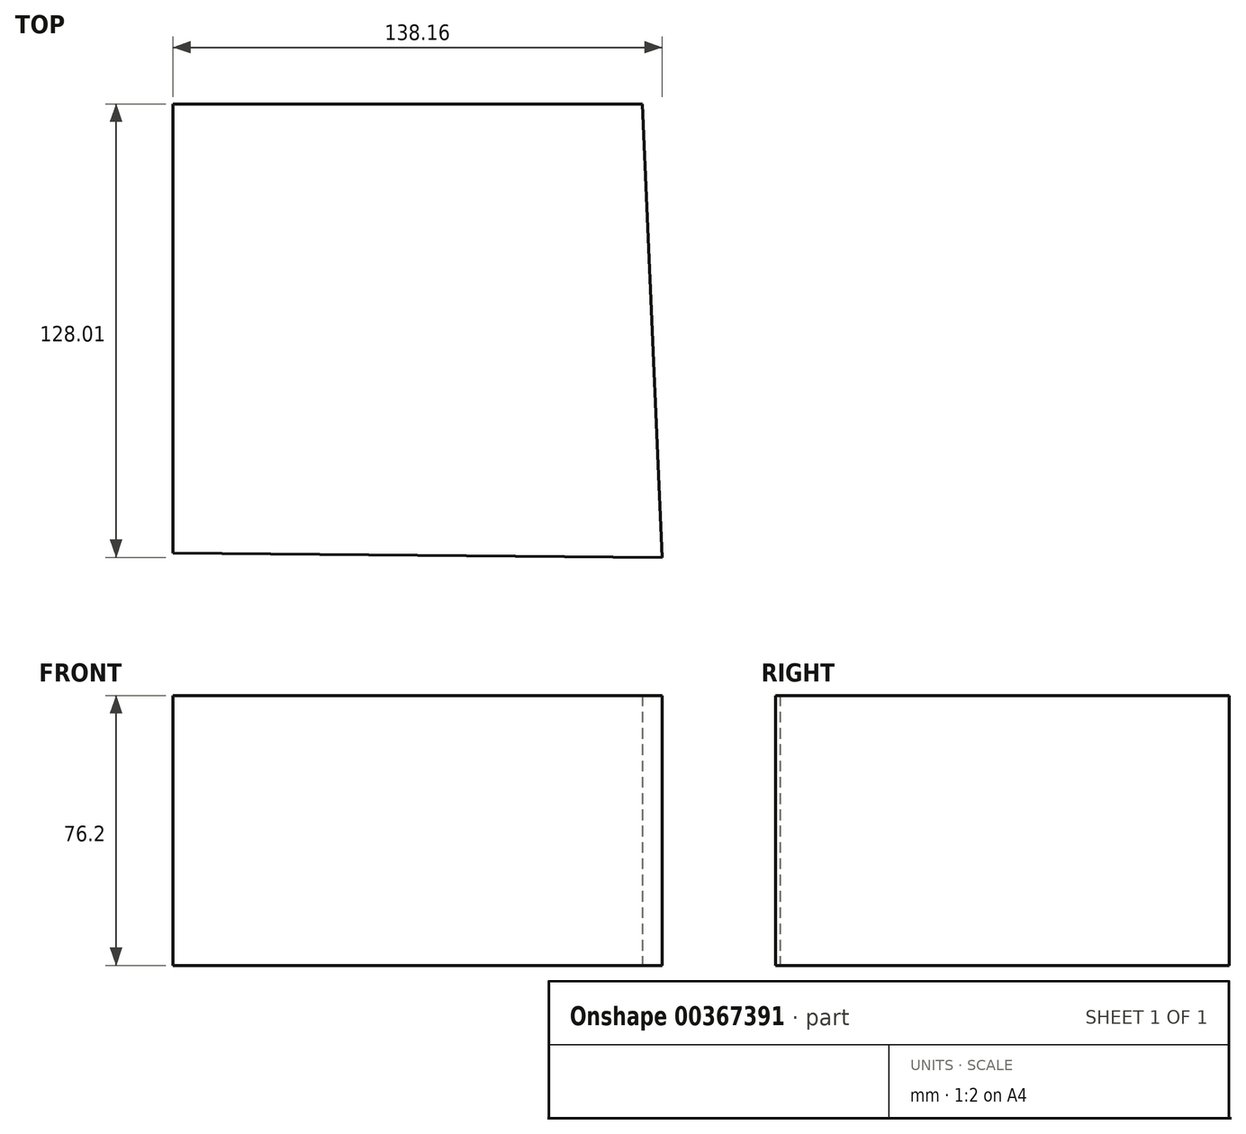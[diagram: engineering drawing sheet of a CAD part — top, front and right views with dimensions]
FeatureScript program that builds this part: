
annotation { "Feature Type Name" : "Feature", "Feature Type Description" : "" }
export const myFeature = defineFeature(function(context is Context, id is Id, definition is map)
    precondition{}
    {
        {
            var Q0;
            Q0=qCreatedBy(makeId("Top.planeOp"),FACE);
            var sketch = newSketch(context, id + "F0", { "sketchPlane" : qUnion([Q0])});
            skLineSegment(sketch, "E0", {"start": v(-138.16, 66.2) * mm, "end": v(-138.16, -60.57) * mm});
            skLineSegment(sketch, "E1", {"start": v(-138.16, 66.2) * mm, "end": v(-5.62, 66.2) * mm});
            skLineSegment(sketch, "E2", {"start": v(-5.62, 66.2) * mm, "end": v(0, -61.81) * mm});
            skLineSegment(sketch, "E3", {"start": v(-138.16, -60.57) * mm, "end": v(0, -61.81) * mm});
            skSolve(sketch);
        }
        {
            var Q0;
            Q0 = qSketchRegion(id + "F0", true);
            extrude(context, id + "F1", {"entities" : qUnion([Q0]), "depth" : 76.2 * mm});
        }
    });
